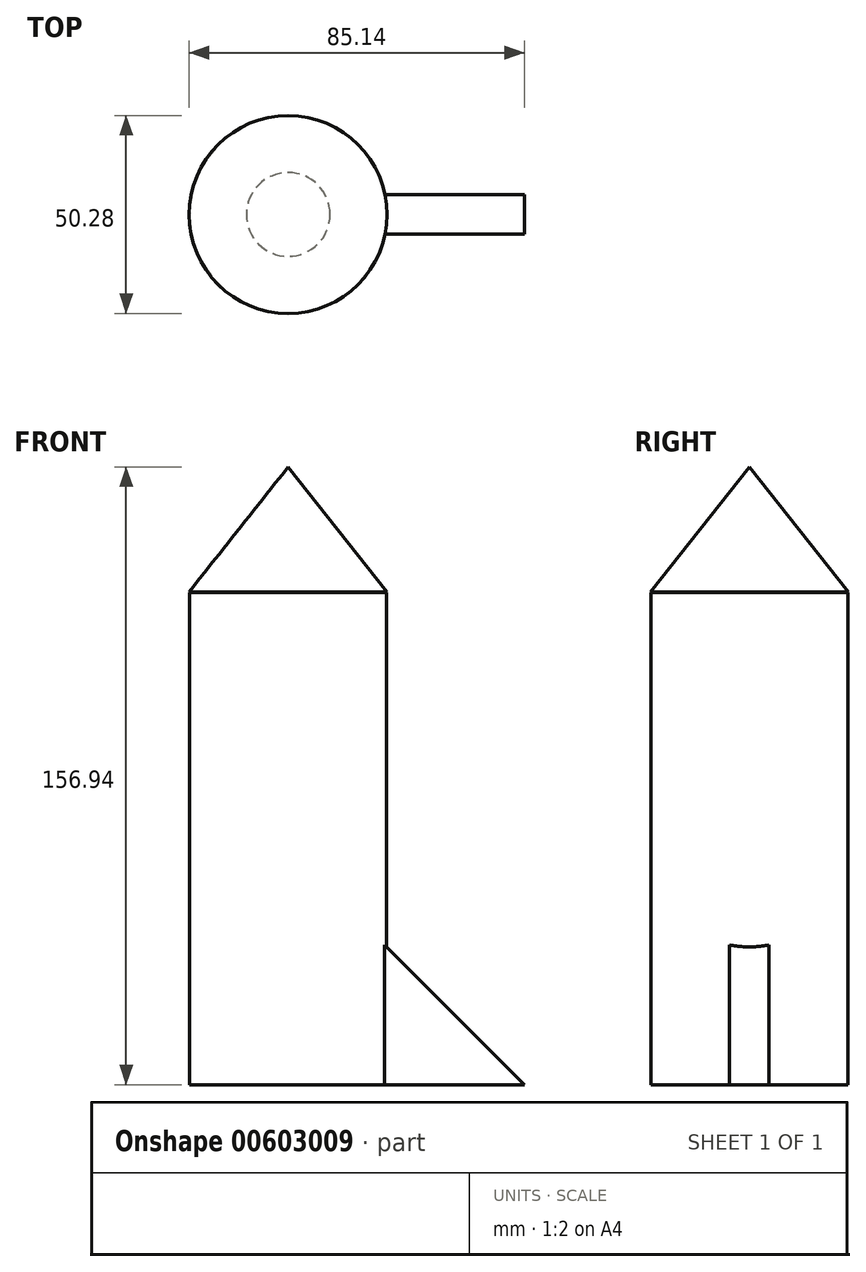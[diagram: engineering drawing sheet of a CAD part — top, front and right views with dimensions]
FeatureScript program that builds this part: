
annotation { "Feature Type Name" : "Feature", "Feature Type Description" : "" }
export const myFeature = defineFeature(function(context is Context, id is Id, definition is map)
    precondition{}
    {
        {
            var Q0;
            Q0=qCreatedBy(makeId("Top.planeOp"),FACE);
            var sketch = newSketch(context, id + "F0", { "sketchPlane" : qUnion([Q0])});
            skCircle(sketch, "E0", {"center": v(0, 0) * mm, "radius": 25 * mm});
            skSolve(sketch);
        }
        {
            var Q0;
            Q0=makeQuery(id+"F0.imprint","IMPRINT",FACE,{"disambiguationData":[TD([[makeQuery(id+"F0.imprint","IMPRINT",EDGE,{"derivedFrom":sQuery(id+"F0.wireOp",EDGE,"E0")}),1.0]])]});
            extrude(context, id + "F1", {"entities" : qUnion([Q0]), "depth" : 125 * mm, "offsetDistance" : 25 * mm});
        }
        {
            var Q0;
            Q0=qCreatedBy(makeId("Front.planeOp"),FACE);
            var sketch = newSketch(context, id + "F2", { "sketchPlane" : qUnion([Q0])});
            skLineSegment(sketch, "E1", {"start": v(0, 0) * mm, "end": v(60, 0) * mm});
            skLineSegment(sketch, "E2", {"start": v(60, 0) * mm, "end": v(0, 60) * mm});
            skLineSegment(sketch, "E3", {"start": v(0, 60) * mm, "end": v(0, 0) * mm});
            skSolve(sketch);
        }
        {
            var Q0;
            Q0=makeQuery(id+"F2.imprint","IMPRINT",FACE,{"disambiguationData":[TD([[makeQuery(id+"F2.imprint","IMPRINT",EDGE,{"derivedFrom":sQuery(id+"F2.wireOp",EDGE,"E1")}),1.0]])]});
            extrude(context, id + "F3", {"entities" : qUnion([Q0]), "operationType" : NewBodyOperationType.ADD, "endBound" : BoundingType.SYMMETRIC, "depth" : 10 * mm, "offsetDistance" : 25 * mm});
        }
        {
            var Q0;
            Q0=qCreatedBy(makeId("Front.planeOp"),FACE);
            var sketch = newSketch(context, id + "F4", { "sketchPlane" : qUnion([Q0])});
            skLineSegment(sketch, "E4", {"start": v(-25.14, 125.23) * mm, "end": v(0, 156.94) * mm});
            skLineSegment(sketch, "E5", {"start": v(0, 156.94) * mm, "end": v(0, 124.83) * mm});
            skLineSegment(sketch, "E6", {"start": v(0, 124.83) * mm, "end": v(-25.14, 125.23) * mm});
            skSolve(sketch);
        }
        {
            var Q0;
            Q0=makeQuery(id+"F4.imprint","IMPRINT",FACE,{"disambiguationData":[TD([[makeQuery(id+"F4.imprint","IMPRINT",EDGE,{"derivedFrom":sQuery(id+"F4.wireOp",EDGE,"E4")}),-1.0]])]});
            var Q1;
            Q1=sQuery(id+"F4.wireOp",EDGE,"E5");
            revolve(context, id + "F5", {"operationType" : NewBodyOperationType.ADD, "entities" : qUnion([Q0]), "axis" : qUnion([Q1]), "revolveType" : RevolveType.FULL});
        }
    });
